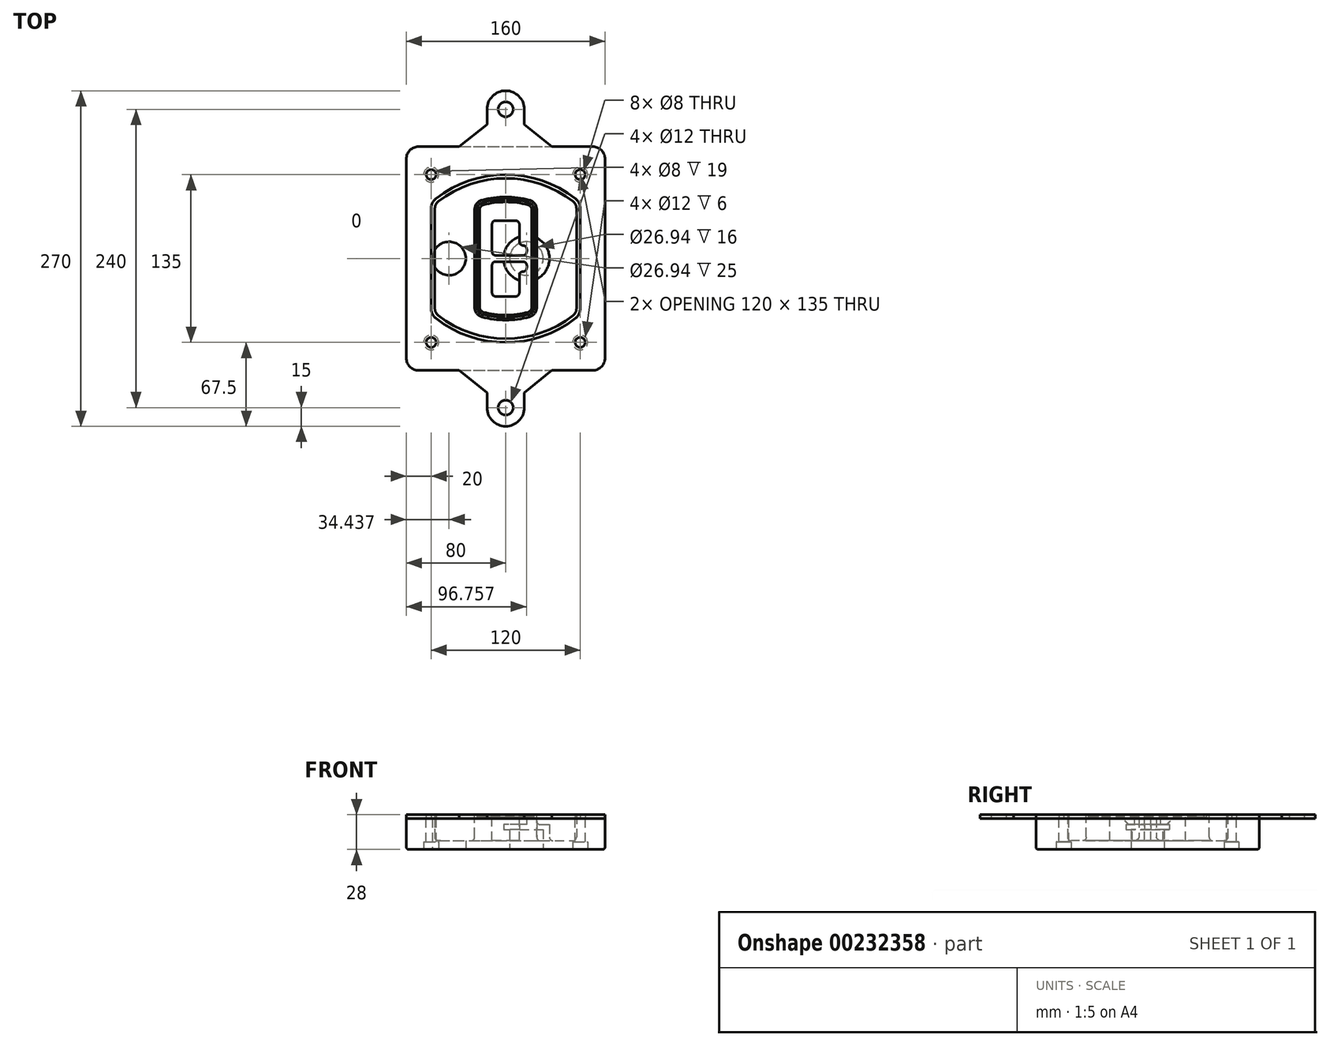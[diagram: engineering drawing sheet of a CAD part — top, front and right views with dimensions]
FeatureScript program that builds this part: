
annotation { "Feature Type Name" : "Feature", "Feature Type Description" : "" }
export const myFeature = defineFeature(function(context is Context, id is Id, definition is map)
    precondition{}
    {
        {
            var Q0;
            Q0=qCreatedBy(makeId("Top.planeOp"),FACE);
            var sketch = newSketch(context, id + "F0", { "sketchPlane" : qUnion([Q0])});
            skPoint(sketch, "E0.rect.middle", {"position": v(0, 0) * mm});
            skLineSegment(sketch, "E1.bottom", {"start": v(-70, -90) * mm, "end": v(70, -90) * mm});
            skLineSegment(sketch, "E1.top", {"start": v(-70, 90) * mm, "end": v(70, 90) * mm});
            skLineSegment(sketch, "E1.left", {"start": v(-80, -80) * mm, "end": v(-80, 80) * mm});
            skLineSegment(sketch, "E1.right", {"start": v(80, -80) * mm, "end": v(80, 80) * mm});
            skLineSegment(sketch, "E2", {"start": v(-80, 90) * mm, "end": v(80, -90) * mm, "construction": true});
            skLineSegment(sketch, "E3", {"start": v(80, 90) * mm, "end": v(-80, -90) * mm, "construction": true});
            skCircle(sketch, "E4", {"center": v(-60, 67.5) * mm, "radius": 4 * mm});
            skCircle(sketch, "E5", {"center": v(60, 67.5) * mm, "radius": 4 * mm});
            skCircle(sketch, "E6", {"center": v(60, -67.5) * mm, "radius": 4 * mm});
            skCircle(sketch, "E7", {"center": v(-60, -67.5) * mm, "radius": 4 * mm});
            skLineSegment(sketch, "E8", {"start": v(-60, 67.5) * mm, "end": v(60, 67.5) * mm, "construction": true});
            skLineSegment(sketch, "E9", {"start": v(60, 67.5) * mm, "end": v(60, -67.5) * mm, "construction": true});
            skLineSegment(sketch, "E10", {"start": v(60, -67.5) * mm, "end": v(-60, -67.5) * mm, "construction": true});
            skLineSegment(sketch, "E11", {"start": v(-60, -67.5) * mm, "end": v(-60, 67.5) * mm, "construction": true});
            skLineSegment(sketch, "E12", {"start": v(-60, 40.3) * mm, "end": v(-60, -40.3) * mm});
            skLineSegment(sketch, "E13", {"start": v(60, 40.3) * mm, "end": v(60, -40.3) * mm});
            skArc(sketch, "E14", {"start": v(56.15, 48.18) * mm, "mid": v(0, 67.5) * mm, "end": v(-56.15, 48.18) * mm});
            skArc(sketch, "E15", {"start": v(-56.15, -48.18) * mm, "mid": v(0, -67.5) * mm, "end": v(56.15, -48.18) * mm});
            skLineSegment(sketch, "E16", {"start": v(-60, 0) * mm, "end": v(60, 0) * mm, "construction": true});
            skPoint(sketch, "E17.visualSharp", {"position": v(-60, -45) * mm});
            skArc(sketch, "E17.filletArc", {"start": v(-60, -40.3) * mm, "mid": v(-58.99, -44.68) * mm, "end": v(-56.15, -48.18) * mm});
            skPoint(sketch, "E18.visualSharp", {"position": v(-60, 45) * mm});
            skArc(sketch, "E18.filletArc", {"start": v(-56.15, 48.18) * mm, "mid": v(-58.99, 44.68) * mm, "end": v(-60, 40.3) * mm});
            skPoint(sketch, "E19.visualSharp", {"position": v(60, 45) * mm});
            skArc(sketch, "E19.filletArc", {"start": v(60, 40.3) * mm, "mid": v(58.99, 44.68) * mm, "end": v(56.15, 48.18) * mm});
            skPoint(sketch, "E20.visualSharp", {"position": v(60, -45) * mm});
            skArc(sketch, "E20.filletArc", {"start": v(56.15, -48.18) * mm, "mid": v(58.99, -44.68) * mm, "end": v(60, -40.3) * mm});
            skPoint(sketch, "E21.visualSharp", {"position": v(-80, 90) * mm});
            skArc(sketch, "E21.filletArc", {"start": v(-70, 90) * mm, "mid": v(-77.07, 87.07) * mm, "end": v(-80, 80) * mm});
            skPoint(sketch, "E22.visualSharp", {"position": v(80, 90) * mm});
            skArc(sketch, "E22.filletArc", {"start": v(80, 80) * mm, "mid": v(77.07, 87.07) * mm, "end": v(70, 90) * mm});
            skPoint(sketch, "E23.visualSharp", {"position": v(80, -90) * mm});
            skArc(sketch, "E23.filletArc", {"start": v(70, -90) * mm, "mid": v(77.07, -87.07) * mm, "end": v(80, -80) * mm});
            skPoint(sketch, "E24.visualSharp", {"position": v(-80, -90) * mm});
            skArc(sketch, "E24.filletArc", {"start": v(-80, -80) * mm, "mid": v(-77.07, -87.07) * mm, "end": v(-70, -90) * mm});
            skArc(sketch, "E25.0", {"start": v(57, 40.3) * mm, "mid": v(56.3, 43.36) * mm, "end": v(54.3, 45.81) * mm});
            skLineSegment(sketch, "E25.1", {"start": v(57, 40.3) * mm, "end": v(57, -40.3) * mm});
            skArc(sketch, "E25.2", {"start": v(54.3, -45.81) * mm, "mid": v(56.3, -43.36) * mm, "end": v(57, -40.3) * mm});
            skArc(sketch, "E25.3", {"start": v(-54.3, -45.81) * mm, "mid": v(0, -64.5) * mm, "end": v(54.3, -45.81) * mm});
            skArc(sketch, "E25.4", {"start": v(-57, -40.3) * mm, "mid": v(-56.3, -43.36) * mm, "end": v(-54.3, -45.81) * mm});
            skArc(sketch, "E25.5", {"start": v(54.3, 45.81) * mm, "mid": v(0, 64.5) * mm, "end": v(-54.3, 45.81) * mm});
            skLineSegment(sketch, "E25.6", {"start": v(-57, 40.3) * mm, "end": v(-57, -40.3) * mm});
            skArc(sketch, "E25.7", {"start": v(-54.3, 45.81) * mm, "mid": v(-56.3, 43.36) * mm, "end": v(-57, 40.3) * mm});
            skArc(sketch, "E26.0", {"start": v(-58.62, 51.33) * mm, "mid": v(-62.58, 46.43) * mm, "end": v(-64, 40.3) * mm});
            skArc(sketch, "E26.1", {"start": v(58.62, 51.33) * mm, "mid": v(0, 71.5) * mm, "end": v(-58.62, 51.33) * mm});
            skArc(sketch, "E26.2", {"start": v(64, 40.3) * mm, "mid": v(62.58, 46.43) * mm, "end": v(58.62, 51.33) * mm});
            skLineSegment(sketch, "E26.3", {"start": v(64, 40.3) * mm, "end": v(64, -40.3) * mm});
            skArc(sketch, "E26.4", {"start": v(58.62, -51.33) * mm, "mid": v(62.58, -46.43) * mm, "end": v(64, -40.3) * mm});
            skLineSegment(sketch, "E26.5", {"start": v(-64, 40.3) * mm, "end": v(-64, -40.3) * mm});
            skArc(sketch, "E26.6", {"start": v(-58.62, -51.33) * mm, "mid": v(0, -71.5) * mm, "end": v(58.62, -51.33) * mm});
            skArc(sketch, "E26.7", {"start": v(-64, -40.3) * mm, "mid": v(-62.58, -46.43) * mm, "end": v(-58.62, -51.33) * mm});
            skSolve(sketch);
        }
        {
            var Q0;
            Q0=makeQuery(id+"F0.imprint","IMPRINT",FACE,{"disambiguationData":[TD([[makeQuery(id+"F0.imprint","IMPRINT",EDGE,{"derivedFrom":sQuery(id+"F0.wireOp",EDGE,"E1.bottom")}),1.0]])]});
            var Q1;
            Q1=makeQuery(id+"F0.imprint","IMPRINT",FACE,{"disambiguationData":[TD([[makeQuery(id+"F0.imprint","IMPRINT",EDGE,{"derivedFrom":sQuery(id+"F0.wireOp",EDGE,"E12")}),1.0]])]});
            var Q2;
            Q2=makeQuery(id+"F0.imprint","IMPRINT",FACE,{"disambiguationData":[TD([[makeQuery(id+"F0.imprint","IMPRINT",EDGE,{"derivedFrom":sQuery(id+"F0.wireOp",EDGE,"E25.0")}),1.0]])]});
            var Q3;
            Q3=makeQuery(id+"F0.imprint","IMPRINT",FACE,{"disambiguationData":[TD([[makeQuery(id+"F0.imprint","IMPRINT",EDGE,{"derivedFrom":sQuery(id+"F0.wireOp",EDGE,"E12")}),-1.0]])]});
            extrude(context, id + "F1", {"entities" : qUnion([Q0, Q1, Q2, Q3]), "oppositeDirection" : true, "depth" : 25 * mm});
        }
        {
            var Q0;
            Q0=makeQuery(id+"F0.imprint","IMPRINT",FACE,{"disambiguationData":[TD([[makeQuery(id+"F0.imprint","IMPRINT",EDGE,{"derivedFrom":sQuery(id+"F0.wireOp",EDGE,"E12")}),1.0]])]});
            extrude(context, id + "F2", {"entities" : qUnion([Q0]), "operationType" : NewBodyOperationType.ADD, "depth" : 3 * mm});
        }
        {
            var Q0;
            Q0=makeQuery(id+"F0.imprint","IMPRINT",FACE,{"disambiguationData":[TD([[makeQuery(id+"F0.imprint","IMPRINT",EDGE,{"derivedFrom":sQuery(id+"F0.wireOp",EDGE,"E25.0")}),1.0]])]});
            extrude(context, id + "F3", {"entities" : qUnion([Q0]), "operationType" : NewBodyOperationType.REMOVE, "oppositeDirection" : true, "depth" : 18 * mm});
        }
        {
            var Q0;
            Q0=makeQuery(id+"F2.opExtrude","CAP_FACE",FACE,{"disambiguationData":[OSD([sQuery(id+"F0.wireOp",EDGE,"E12"),sQuery(id+"F0.wireOp",EDGE,"E13"),sQuery(id+"F0.wireOp",EDGE,"E14"),sQuery(id+"F0.wireOp",EDGE,"E15"),sQuery(id+"F0.wireOp",EDGE,"E17.filletArc"),sQuery(id+"F0.wireOp",EDGE,"E18.filletArc"),sQuery(id+"F0.wireOp",EDGE,"E19.filletArc"),sQuery(id+"F0.wireOp",EDGE,"E20.filletArc"),sQuery(id+"F0.wireOp",EDGE,"E25.0"),sQuery(id+"F0.wireOp",EDGE,"E25.1"),sQuery(id+"F0.wireOp",EDGE,"E25.2"),sQuery(id+"F0.wireOp",EDGE,"E25.3"),sQuery(id+"F0.wireOp",EDGE,"E25.4"),sQuery(id+"F0.wireOp",EDGE,"E25.5"),sQuery(id+"F0.wireOp",EDGE,"E25.6"),sQuery(id+"F0.wireOp",EDGE,"E25.7")])],"isStart":false});
            var sketch = newSketch(context, id + "F4", { "sketchPlane" : qUnion([Q0])});
            skArc(sketch, "E27.0", {"start": v(-19.08, -46.97) * mm, "mid": v(0, -49.5) * mm, "end": v(19.08, -46.97) * mm});
            skArc(sketch, "E28.0", {"start": v(19.08, 46.97) * mm, "mid": v(0, 49.5) * mm, "end": v(-19.08, 46.97) * mm});
            skLineSegment(sketch, "E29", {"start": v(-25, 39.25) * mm, "end": v(-25, -39.25) * mm});
            skLineSegment(sketch, "E30", {"start": v(25, 39.25) * mm, "end": v(25, -39.25) * mm});
            skLineSegment(sketch, "E31", {"start": v(-25, 45.1) * mm, "end": v(25, 45.1) * mm, "construction": true});
            skLineSegment(sketch, "E32", {"start": v(-25, -45.1) * mm, "end": v(25, -45.1) * mm, "construction": true});
            skPoint(sketch, "E33.visualSharp", {"position": v(-25, 45.1) * mm});
            skArc(sketch, "E33.filletArc", {"start": v(-19.08, 46.97) * mm, "mid": v(-23.35, 44.11) * mm, "end": v(-25, 39.25) * mm});
            skPoint(sketch, "E34.visualSharp", {"position": v(25, 45.1) * mm});
            skArc(sketch, "E34.filletArc", {"start": v(25, 39.25) * mm, "mid": v(23.35, 44.11) * mm, "end": v(19.08, 46.97) * mm});
            skPoint(sketch, "E35.visualSharp", {"position": v(25, -45.1) * mm});
            skArc(sketch, "E35.filletArc", {"start": v(19.08, -46.97) * mm, "mid": v(23.35, -44.11) * mm, "end": v(25, -39.25) * mm});
            skPoint(sketch, "E36.visualSharp", {"position": v(-25, -45.1) * mm});
            skArc(sketch, "E36.filletArc", {"start": v(-25, -39.25) * mm, "mid": v(-23.35, -44.11) * mm, "end": v(-19.08, -46.97) * mm});
            skArc(sketch, "E37.0", {"start": v(54.3, 45.81) * mm, "mid": v(0, 64.5) * mm, "end": v(-54.3, 45.81) * mm});
            skArc(sketch, "E37.1", {"start": v(-54.3, 45.81) * mm, "mid": v(-56.3, 43.36) * mm, "end": v(-57, 40.3) * mm});
            skLineSegment(sketch, "E37.2", {"start": v(-57, 40.3) * mm, "end": v(-57, -40.3) * mm});
            skArc(sketch, "E37.3", {"start": v(-57, -40.3) * mm, "mid": v(-56.3, -43.36) * mm, "end": v(-54.3, -45.81) * mm});
            skArc(sketch, "E37.4", {"start": v(-54.3, -45.81) * mm, "mid": v(0, -64.5) * mm, "end": v(54.3, -45.81) * mm});
            skArc(sketch, "E37.5", {"start": v(54.3, -45.81) * mm, "mid": v(56.3, -43.36) * mm, "end": v(57, -40.3) * mm});
            skLineSegment(sketch, "E37.6", {"start": v(57, 40.3) * mm, "end": v(57, -40.3) * mm});
            skArc(sketch, "E37.7", {"start": v(57, 40.3) * mm, "mid": v(56.3, 43.36) * mm, "end": v(54.3, 45.81) * mm});
            skLineSegment(sketch, "E38.0", {"start": v(23, 39.25) * mm, "end": v(23, -39.25) * mm});
            skArc(sketch, "E38.1", {"start": v(18.56, -45.04) * mm, "mid": v(21.76, -42.9) * mm, "end": v(23, -39.25) * mm});
            skArc(sketch, "E38.2", {"start": v(-18.56, -45.04) * mm, "mid": v(0, -47.5) * mm, "end": v(18.56, -45.04) * mm});
            skArc(sketch, "E38.3", {"start": v(-23, -39.25) * mm, "mid": v(-21.76, -42.9) * mm, "end": v(-18.56, -45.04) * mm});
            skLineSegment(sketch, "E38.4", {"start": v(-23, 39.25) * mm, "end": v(-23, -39.25) * mm});
            skArc(sketch, "E38.5", {"start": v(23, 39.25) * mm, "mid": v(21.76, 42.9) * mm, "end": v(18.56, 45.04) * mm});
            skArc(sketch, "E38.6", {"start": v(-18.56, 45.04) * mm, "mid": v(-21.76, 42.9) * mm, "end": v(-23, 39.25) * mm});
            skArc(sketch, "E38.7", {"start": v(18.56, 45.04) * mm, "mid": v(0, 47.5) * mm, "end": v(-18.56, 45.04) * mm});
            skArc(sketch, "E39.0", {"start": v(21, 39.25) * mm, "mid": v(20.18, 41.68) * mm, "end": v(18.04, 43.1) * mm});
            skLineSegment(sketch, "E39.1", {"start": v(21, 39.25) * mm, "end": v(21, -39.25) * mm});
            skArc(sketch, "E39.2", {"start": v(18.04, -43.1) * mm, "mid": v(20.18, -41.68) * mm, "end": v(21, -39.25) * mm});
            skArc(sketch, "E39.3", {"start": v(-18.04, -43.1) * mm, "mid": v(0, -45.5) * mm, "end": v(18.04, -43.1) * mm});
            skArc(sketch, "E39.4", {"start": v(-21, -39.25) * mm, "mid": v(-20.18, -41.68) * mm, "end": v(-18.04, -43.1) * mm});
            skArc(sketch, "E39.5", {"start": v(18.04, 43.1) * mm, "mid": v(0, 45.5) * mm, "end": v(-18.04, 43.1) * mm});
            skLineSegment(sketch, "E39.6", {"start": v(-21, 39.25) * mm, "end": v(-21, -39.25) * mm});
            skArc(sketch, "E39.7", {"start": v(-18.04, 43.1) * mm, "mid": v(-20.18, 41.68) * mm, "end": v(-21, 39.25) * mm});
            skLineSegment(sketch, "E40", {"start": v(-25, 0) * mm, "end": v(25, 0) * mm, "construction": true});
            skLineSegment(sketch, "E41", {"start": v(-11, 5.5) * mm, "end": v(-11, 27.5) * mm});
            skLineSegment(sketch, "E42", {"start": v(-8, 30.5) * mm, "end": v(8, 30.5) * mm});
            skLineSegment(sketch, "E43", {"start": v(11, 27.5) * mm, "end": v(11, 13.5) * mm});
            skLineSegment(sketch, "E44", {"start": v(14, 10.5) * mm, "end": v(14, 10.5) * mm});
            skLineSegment(sketch, "E45", {"start": v(17, 7.5) * mm, "end": v(17, 5.5) * mm});
            skLineSegment(sketch, "E46", {"start": v(14, 2.5) * mm, "end": v(-8, 2.5) * mm});
            skPoint(sketch, "E47.visualSharp", {"position": v(-11, 30.5) * mm});
            skArc(sketch, "E47.filletArc", {"start": v(-8, 30.5) * mm, "mid": v(-10.12, 29.62) * mm, "end": v(-11, 27.5) * mm});
            skPoint(sketch, "E48.visualSharp", {"position": v(11, 30.5) * mm});
            skArc(sketch, "E48.filletArc", {"start": v(11, 27.5) * mm, "mid": v(10.12, 29.62) * mm, "end": v(8, 30.5) * mm});
            skPoint(sketch, "E49.visualSharp", {"position": v(11, 10.5) * mm});
            skArc(sketch, "E49.filletArc", {"start": v(11, 13.5) * mm, "mid": v(11.88, 11.38) * mm, "end": v(14, 10.5) * mm});
            skPoint(sketch, "E50.visualSharp", {"position": v(17, 10.5) * mm});
            skArc(sketch, "E50.filletArc", {"start": v(17, 7.5) * mm, "mid": v(16.12, 9.62) * mm, "end": v(14, 10.5) * mm});
            skPoint(sketch, "E51.visualSharp", {"position": v(17, 2.5) * mm});
            skArc(sketch, "E51.filletArc", {"start": v(14, 2.5) * mm, "mid": v(16.12, 3.38) * mm, "end": v(17, 5.5) * mm});
            skPoint(sketch, "E52.visualSharp", {"position": v(-11, 2.5) * mm});
            skArc(sketch, "E52.filletArc", {"start": v(-11, 5.5) * mm, "mid": v(-10.12, 3.38) * mm, "end": v(-8, 2.5) * mm});
            skLineSegment(sketch, "E53.0.MirrorCS", {"start": v(14, -2.5) * mm, "end": v(-8, -2.5) * mm});
            skArc(sketch, "E54.0.MirrorCS", {"start": v(-11, -5.5) * mm, "mid": v(-10.12, -3.38) * mm, "end": v(-8, -2.5) * mm});
            skLineSegment(sketch, "E55.0.MirrorCS", {"start": v(-11, -5.5) * mm, "end": v(-11, -27.5) * mm});
            skArc(sketch, "E56.0.MirrorCS", {"start": v(-8, -30.5) * mm, "mid": v(-10.12, -29.62) * mm, "end": v(-11, -27.5) * mm});
            skLineSegment(sketch, "E57.0.MirrorCS", {"start": v(-8, -30.5) * mm, "end": v(8, -30.5) * mm});
            skArc(sketch, "E58.0.MirrorCS", {"start": v(11, -27.5) * mm, "mid": v(10.12, -29.62) * mm, "end": v(8, -30.5) * mm});
            skLineSegment(sketch, "E59.0.MirrorCS", {"start": v(11, -27.5) * mm, "end": v(11, -13.5) * mm});
            skArc(sketch, "E60.0.MirrorCS", {"start": v(11, -13.5) * mm, "mid": v(11.88, -11.38) * mm, "end": v(14, -10.5) * mm});
            skArc(sketch, "E61.0.MirrorCS", {"start": v(17, -7.5) * mm, "mid": v(16.12, -9.62) * mm, "end": v(14, -10.5) * mm});
            skLineSegment(sketch, "E62.0.MirrorCS", {"start": v(17, -7.5) * mm, "end": v(17, -5.5) * mm});
            skArc(sketch, "E63.0.MirrorCS", {"start": v(14, -2.5) * mm, "mid": v(16.12, -3.38) * mm, "end": v(17, -5.5) * mm});
            skSolve(sketch);
        }
        {
            var Q0;
            Q0=makeQuery(id+"F4.imprint","IMPRINT",FACE,{"disambiguationData":[TD([[makeQuery(id+"F4.imprint","IMPRINT",EDGE,{"derivedFrom":sQuery(id+"F4.wireOp",EDGE,"E27.0")}),1.0]])]});
            var Q1;
            Q1=makeQuery(id+"F4.imprint","IMPRINT",FACE,{"disambiguationData":[TD([[makeQuery(id+"F4.imprint","IMPRINT",EDGE,{"derivedFrom":sQuery(id+"F4.wireOp",EDGE,"E38.0")}),-1.0]])]});
            var Q2;
            Q2=makeQuery(id+"F4.imprint","IMPRINT",FACE,{"disambiguationData":[TD([[makeQuery(id+"F4.imprint","IMPRINT",EDGE,{"derivedFrom":sQuery(id+"F4.wireOp",EDGE,"E39.0")}),1.0]])]});
            extrude(context, id + "F5", {"entities" : qUnion([Q0, Q1, Q2]), "operationType" : NewBodyOperationType.ADD, "endBound" : BoundingType.UP_TO_NEXT, "oppositeDirection" : true, "depth" : 25 * mm});
        }
        {
            var Q0;
            Q0=makeQuery(id+"F4.imprint","IMPRINT",FACE,{"disambiguationData":[TD([[makeQuery(id+"F4.imprint","IMPRINT",EDGE,{"derivedFrom":sQuery(id+"F4.wireOp",EDGE,"E38.0")}),-1.0]])]});
            extrude(context, id + "F6", {"entities" : qUnion([Q0]), "operationType" : NewBodyOperationType.REMOVE, "oppositeDirection" : true, "depth" : 2 * mm});
        }
        {
            var Q0;
            Q0=makeQuery(id+"F1.opExtrude","CAP_FACE",FACE,{"disambiguationData":[OSD([sQuery(id+"F0.wireOp",EDGE,"E1.bottom"),sQuery(id+"F0.wireOp",EDGE,"E1.top"),sQuery(id+"F0.wireOp",EDGE,"E1.left"),sQuery(id+"F0.wireOp",EDGE,"E1.right"),sQuery(id+"F0.wireOp",EDGE,"E4"),sQuery(id+"F0.wireOp",EDGE,"E5"),sQuery(id+"F0.wireOp",EDGE,"E6"),sQuery(id+"F0.wireOp",EDGE,"E7"),sQuery(id+"F0.wireOp",EDGE,"E21.filletArc"),sQuery(id+"F0.wireOp",EDGE,"E22.filletArc"),sQuery(id+"F0.wireOp",EDGE,"E23.filletArc"),sQuery(id+"F0.wireOp",EDGE,"E24.filletArc")])],"isStart":false});
            var sketch = newSketch(context, id + "F7", { "sketchPlane" : qUnion([Q0])});
            skCircle(sketch, "E64", {"center": v(16.76, 0) * mm, "radius": 13.47 * mm});
            skCircle(sketch, "E65", {"center": v(-45.56, 0) * mm, "radius": 13.47 * mm});
            skLineSegment(sketch, "E66", {"start": v(80, 0) * mm, "end": v(-80, 0) * mm});
            skCircle(sketch, "E67", {"center": v(16.76, 0) * mm, "radius": 18.47 * mm});
            skCircle(sketch, "E68", {"center": v(60, -67.5) * mm, "radius": 6 * mm});
            skCircle(sketch, "E69", {"center": v(-60, -67.5) * mm, "radius": 6 * mm});
            skCircle(sketch, "E70", {"center": v(-60, 67.5) * mm, "radius": 6 * mm});
            skCircle(sketch, "E71", {"center": v(60, 67.5) * mm, "radius": 6 * mm});
            skSolve(sketch);
        }
        {
            var Q0;
            {var subQ1=sQuery(id+"F7.wireOp",EDGE,"E66");var subQ4=sQuery(id+"F7.wireOp",EDGE,"E64");var subQ6=makeQuery(id+"F7.imprint","INTERSECT",VERTEX,{"disambiguationData":[OD(0.0)],"derivedFrom":[subQ4,subQ1]});Q0=makeQuery(id+"F7.imprint","IMPRINT",FACE,{"disambiguationData":[TD([[makeQuery(id+"F7.imprint","IMPRINT",EDGE,{"disambiguationData":[TD([[subQ6,-1.0]])],"derivedFrom":subQ4}),-1.0]])]});}
            var Q1;
            {var subQ0=sQuery(id+"F7.wireOp",EDGE,"E66");var subQ1=sQuery(id+"F7.wireOp",EDGE,"E64");var subQ3=makeQuery(id+"F7.imprint","INTERSECT",VERTEX,{"disambiguationData":[OD(0.0)],"derivedFrom":[subQ1,subQ0]});Q1=makeQuery(id+"F7.imprint","IMPRINT",FACE,{"disambiguationData":[TD([[makeQuery(id+"F7.imprint","IMPRINT",EDGE,{"disambiguationData":[TD([[subQ3,-1.0]])],"derivedFrom":subQ1}),1.0]])]});}
            var Q2;
            {var subQ0=sQuery(id+"F7.wireOp",EDGE,"E66");var subQ1=sQuery(id+"F7.wireOp",EDGE,"E64");var subQ3=makeQuery(id+"F7.imprint","INTERSECT",VERTEX,{"disambiguationData":[OD(0.0)],"derivedFrom":[subQ1,subQ0]});Q2=makeQuery(id+"F7.imprint","IMPRINT",FACE,{"disambiguationData":[TD([[makeQuery(id+"F7.imprint","IMPRINT",EDGE,{"disambiguationData":[TD([[subQ3,1.0]])],"derivedFrom":subQ1}),1.0]])]});}
            var Q3;
            {var subQ1=sQuery(id+"F7.wireOp",EDGE,"E66");var subQ4=sQuery(id+"F7.wireOp",EDGE,"E64");var subQ6=makeQuery(id+"F7.imprint","INTERSECT",VERTEX,{"disambiguationData":[OD(0.0)],"derivedFrom":[subQ4,subQ1]});Q3=makeQuery(id+"F7.imprint","IMPRINT",FACE,{"disambiguationData":[TD([[makeQuery(id+"F7.imprint","IMPRINT",EDGE,{"disambiguationData":[TD([[subQ6,1.0]])],"derivedFrom":subQ4}),-1.0]])]});}
            extrude(context, id + "F8", {"entities" : qUnion([Q0, Q1, Q2, Q3]), "operationType" : NewBodyOperationType.ADD, "oppositeDirection" : true, "depth" : 20 * mm});
        }
        {
            var Q0;
            {var subQ0=sQuery(id+"F7.wireOp",EDGE,"E66");var subQ1=sQuery(id+"F7.wireOp",EDGE,"E64");var subQ3=makeQuery(id+"F7.imprint","INTERSECT",VERTEX,{"disambiguationData":[OD(0.0)],"derivedFrom":[subQ1,subQ0]});Q0=makeQuery(id+"F7.imprint","IMPRINT",FACE,{"disambiguationData":[TD([[makeQuery(id+"F7.imprint","IMPRINT",EDGE,{"disambiguationData":[TD([[subQ3,-1.0]])],"derivedFrom":subQ1}),1.0]])]});}
            var Q1;
            {var subQ0=sQuery(id+"F7.wireOp",EDGE,"E66");var subQ1=sQuery(id+"F7.wireOp",EDGE,"E64");var subQ3=makeQuery(id+"F7.imprint","INTERSECT",VERTEX,{"disambiguationData":[OD(0.0)],"derivedFrom":[subQ1,subQ0]});Q1=makeQuery(id+"F7.imprint","IMPRINT",FACE,{"disambiguationData":[TD([[makeQuery(id+"F7.imprint","IMPRINT",EDGE,{"disambiguationData":[TD([[subQ3,1.0]])],"derivedFrom":subQ1}),1.0]])]});}
            extrude(context, id + "F9", {"entities" : qUnion([Q0, Q1]), "operationType" : NewBodyOperationType.REMOVE, "oppositeDirection" : true, "depth" : 16 * mm});
        }
        {
            var Q0;
            {var subQ0=sQuery(id+"F7.wireOp",EDGE,"E66");var subQ1=sQuery(id+"F7.wireOp",EDGE,"E65");var subQ3=makeQuery(id+"F7.imprint","INTERSECT",VERTEX,{"disambiguationData":[OD(0.0)],"derivedFrom":[subQ1,subQ0]});Q0=makeQuery(id+"F7.imprint","IMPRINT",FACE,{"disambiguationData":[TD([[makeQuery(id+"F7.imprint","IMPRINT",EDGE,{"disambiguationData":[TD([[subQ3,-1.0]])],"derivedFrom":subQ1}),1.0]])]});}
            var Q1;
            {var subQ0=sQuery(id+"F7.wireOp",EDGE,"E66");var subQ1=sQuery(id+"F7.wireOp",EDGE,"E65");var subQ3=makeQuery(id+"F7.imprint","INTERSECT",VERTEX,{"disambiguationData":[OD(0.0)],"derivedFrom":[subQ1,subQ0]});Q1=makeQuery(id+"F7.imprint","IMPRINT",FACE,{"disambiguationData":[TD([[makeQuery(id+"F7.imprint","IMPRINT",EDGE,{"disambiguationData":[TD([[subQ3,1.0]])],"derivedFrom":subQ1}),1.0]])]});}
            extrude(context, id + "F10", {"entities" : qUnion([Q0, Q1]), "operationType" : NewBodyOperationType.REMOVE, "oppositeDirection" : true, "depth" : 25 * mm});
        }
        {
            var Q0;
            Q0=makeQuery(id+"F7.imprint","IMPRINT",FACE,{"disambiguationData":[TD([[makeQuery(id+"F7.imprint","IMPRINT",EDGE,{"derivedFrom":sQuery(id+"F7.wireOp",EDGE,"E68")}),1.0]])]});
            var Q1;
            Q1=makeQuery(id+"F7.imprint","IMPRINT",FACE,{"disambiguationData":[TD([[makeQuery(id+"F7.imprint","IMPRINT",EDGE,{"derivedFrom":makeQuery(id+"F1.opExtrude","CAP_EDGE",EDGE,{"disambiguationData":[OSD([sQuery(id+"F0.wireOp",EDGE,"E5")])],"isStart":false})}),-1.0]])]});
            var Q2;
            Q2=makeQuery(id+"F7.imprint","IMPRINT",FACE,{"disambiguationData":[TD([[makeQuery(id+"F7.imprint","IMPRINT",EDGE,{"derivedFrom":sQuery(id+"F7.wireOp",EDGE,"E69")}),1.0]])]});
            var Q3;
            Q3=makeQuery(id+"F7.imprint","IMPRINT",FACE,{"disambiguationData":[TD([[makeQuery(id+"F7.imprint","IMPRINT",EDGE,{"derivedFrom":makeQuery(id+"F1.opExtrude","CAP_EDGE",EDGE,{"disambiguationData":[OSD([sQuery(id+"F0.wireOp",EDGE,"E4")])],"isStart":false})}),-1.0]])]});
            var Q4;
            Q4=makeQuery(id+"F7.imprint","IMPRINT",FACE,{"disambiguationData":[TD([[makeQuery(id+"F7.imprint","IMPRINT",EDGE,{"derivedFrom":sQuery(id+"F7.wireOp",EDGE,"E70")}),1.0]])]});
            var Q5;
            Q5=makeQuery(id+"F7.imprint","IMPRINT",FACE,{"disambiguationData":[TD([[makeQuery(id+"F7.imprint","IMPRINT",EDGE,{"derivedFrom":makeQuery(id+"F1.opExtrude","CAP_EDGE",EDGE,{"disambiguationData":[OSD([sQuery(id+"F0.wireOp",EDGE,"E7")])],"isStart":false})}),-1.0]])]});
            var Q6;
            Q6=makeQuery(id+"F7.imprint","IMPRINT",FACE,{"disambiguationData":[TD([[makeQuery(id+"F7.imprint","IMPRINT",EDGE,{"derivedFrom":sQuery(id+"F7.wireOp",EDGE,"E71")}),1.0]])]});
            var Q7;
            Q7=makeQuery(id+"F7.imprint","IMPRINT",FACE,{"disambiguationData":[TD([[makeQuery(id+"F7.imprint","IMPRINT",EDGE,{"derivedFrom":makeQuery(id+"F1.opExtrude","CAP_EDGE",EDGE,{"disambiguationData":[OSD([sQuery(id+"F0.wireOp",EDGE,"E6")])],"isStart":false})}),-1.0]])]});
            extrude(context, id + "F11", {"entities" : qUnion([Q0, Q1, Q2, Q3, Q4, Q5, Q6, Q7]), "operationType" : NewBodyOperationType.REMOVE, "oppositeDirection" : true, "depth" : 6 * mm});
        }
        {
            var Q0;
            Q0=makeQuery(id+"F9.boolean.opBoolean","COPY",FACE,{"derivedFrom":makeQuery(id+"F9.opExtrude","CAP_FACE",FACE,{"disambiguationData":[OSD([sQuery(id+"F7.wireOp",EDGE,"E64")])],"isStart":false})});
            var sketch = newSketch(context, id + "F12", { "sketchPlane" : qUnion([Q0])});
            skArc(sketch, "E72.0", {"start": v(11, 17.55) * mm, "mid": v(2.57, 11.82) * mm, "end": v(-1.54, 2.5) * mm});
            skArc(sketch, "E72.1", {"start": v(-1.54, -2.5) * mm, "mid": v(2.57, -11.82) * mm, "end": v(11, -17.55) * mm});
            skLineSegment(sketch, "E73", {"start": v(-1.54, -2.5) * mm, "end": v(14, -2.5) * mm});
            skLineSegment(sketch, "E74.0", {"start": v(14, 2.5) * mm, "end": v(-1.54, 2.5) * mm});
            skArc(sketch, "E74.1", {"start": v(14, 2.5) * mm, "mid": v(16.12, 3.38) * mm, "end": v(17, 5.5) * mm});
            skLineSegment(sketch, "E74.2", {"start": v(17, 7.5) * mm, "end": v(17, 5.5) * mm});
            skArc(sketch, "E74.3", {"start": v(17, 7.5) * mm, "mid": v(16.12, 9.62) * mm, "end": v(14, 10.5) * mm});
            skArc(sketch, "E74.4", {"start": v(11, 13.5) * mm, "mid": v(11.88, 11.38) * mm, "end": v(14, 10.5) * mm});
            skLineSegment(sketch, "E74.5", {"start": v(11, 17.55) * mm, "end": v(11, 13.5) * mm});
            skLineSegment(sketch, "E74.7", {"start": v(14, -2.5) * mm, "end": v(-1.54, -2.5) * mm});
            skArc(sketch, "E74.8", {"start": v(14, -2.5) * mm, "mid": v(16.12, -3.38) * mm, "end": v(17, -5.5) * mm});
            skLineSegment(sketch, "E74.9", {"start": v(17, -7.5) * mm, "end": v(17, -5.5) * mm});
            skArc(sketch, "E74.10", {"start": v(17, -7.5) * mm, "mid": v(16.12, -9.62) * mm, "end": v(14, -10.5) * mm});
            skArc(sketch, "E74.11", {"start": v(11, -13.5) * mm, "mid": v(11.88, -11.38) * mm, "end": v(14, -10.5) * mm});
            skLineSegment(sketch, "E74.12", {"start": v(11, -17.55) * mm, "end": v(11, -13.5) * mm});
            skPoint(sketch, "E75.orphan", {"position": v(11, -27.5) * mm});
            skPoint(sketch, "E76.orphan", {"position": v(-8, -2.5) * mm});
            skPoint(sketch, "E77.orphan", {"position": v(-8, 2.5) * mm});
            skPoint(sketch, "E78.orphan", {"position": v(11, 27.5) * mm});
            skSolve(sketch);
        }
        {
            var Q0;
            {var subQ7=sQuery(id+"F12.wireOp",EDGE,"E72.0");var subQ14=sQuery(id+"F12.wireOp",EDGE,"E72.1");var subQ16=sQuery(id+"F12.wireOp",EDGE,"E74.1");var subQ18=sQuery(id+"F12.wireOp",EDGE,"E74.8");Q0=qUnion([makeQuery(id+"F12.imprint","IMPRINT",FACE,{"disambiguationData":[TD([[makeQuery(id+"F12.imprint","IMPRINT",EDGE,{"derivedFrom":subQ7}),1.0]])]}),makeQuery(id+"F12.imprint","IMPRINT",FACE,{"disambiguationData":[TD([[makeQuery(id+"F12.imprint","IMPRINT",EDGE,{"derivedFrom":subQ14}),1.0]])]}),makeQuery(id+"F12.imprint","IMPRINT",FACE,{"disambiguationData":[TD([[makeQuery(id+"F12.imprint","IMPRINT",EDGE,{"derivedFrom":subQ16}),1.0]])]}),makeQuery(id+"F12.imprint","IMPRINT",FACE,{"disambiguationData":[TD([[makeQuery(id+"F12.imprint","IMPRINT",EDGE,{"derivedFrom":subQ18}),-1.0]])]})]);}
            var Q1;
            Q1=makeQuery(id+"F5.boolean.opBoolean","SPLIT",FACE,{"disambiguationData":[TD([makeQuery(id+"F5.opExtrude","SWEPT_FACE",FACE,{"disambiguationData":[OSD([sQuery(id+"F4.wireOp",EDGE,"E41")])]})])],"derivedFrom":makeQuery(id+"F3.boolean.opBoolean","COPY",FACE,{"derivedFrom":makeQuery(id+"F3.opExtrude","CAP_FACE",FACE,{"disambiguationData":[OSD([sQuery(id+"F0.wireOp",EDGE,"E25.0"),sQuery(id+"F0.wireOp",EDGE,"E25.1"),sQuery(id+"F0.wireOp",EDGE,"E25.2"),sQuery(id+"F0.wireOp",EDGE,"E25.3"),sQuery(id+"F0.wireOp",EDGE,"E25.4"),sQuery(id+"F0.wireOp",EDGE,"E25.5"),sQuery(id+"F0.wireOp",EDGE,"E25.6"),sQuery(id+"F0.wireOp",EDGE,"E25.7")])],"isStart":false})})});
            extrude(context, id + "F13", {"entities" : qUnion([Q0]), "operationType" : NewBodyOperationType.REMOVE, "endBound" : BoundingType.UP_TO_SURFACE, "endBoundEntityFace" : qUnion([Q1]), "depth" : 25 * mm});
        }
        {
            var Q0;
            Q0=makeQuery(id+"F3.boolean.opBoolean","COPY",EDGE,{"derivedFrom":makeQuery(id+"F3.opExtrude","CAP_EDGE",EDGE,{"disambiguationData":[OSD([sQuery(id+"F0.wireOp",EDGE,"E25.6")])],"isStart":false})});
            var Q1;
            Q1=makeQuery(id+"F8.boolean.opBoolean","INTERSECT",EDGE,{"derivedFrom":[makeQuery(id+"F5.opExtrude","SWEPT_FACE",FACE,{"disambiguationData":[OSD([sQuery(id+"F4.wireOp",EDGE,"E30")])]}),makeQuery(id+"F8.opExtrude","CAP_FACE",FACE,{"disambiguationData":[OSD([sQuery(id+"F7.wireOp",EDGE,"E67")])],"isStart":false})]});
            var Q2;
            Q2=makeQuery(id+"F8.boolean.opBoolean","INTERSECT",EDGE,{"disambiguationData":[OD(1.0)],"derivedFrom":[makeQuery(id+"F5.opExtrude","SWEPT_FACE",FACE,{"disambiguationData":[OSD([sQuery(id+"F4.wireOp",EDGE,"E30")])]}),makeQuery(id+"F8.opExtrude","SWEPT_FACE",FACE,{"disambiguationData":[OSD([sQuery(id+"F7.wireOp",EDGE,"E67")])]})]});
            var Q3;
            {var subQ0=sQuery(id+"F4.wireOp",EDGE,"E30");Q3=makeQuery(id+"F8.boolean.opBoolean","SPLIT",EDGE,{"disambiguationData":[TD([makeQuery(id+"F5.opExtrude","SWEPT_FACE",FACE,{"disambiguationData":[OSD([sQuery(id+"F4.wireOp",EDGE,"E35.filletArc")])]})])],"derivedFrom":makeQuery(id+"F5.opExtrude","CAP_EDGE",EDGE,{"disambiguationData":[OSD([subQ0])],"isStart":false})});}
            var Q4;
            {var subQ0=sQuery(id+"F0.wireOp",EDGE,"E25.7");var subQ1=sQuery(id+"F0.wireOp",EDGE,"E25.1");var subQ2=sQuery(id+"F0.wireOp",EDGE,"E25.6");var subQ3=sQuery(id+"F0.wireOp",EDGE,"E25.5");var subQ4=sQuery(id+"F0.wireOp",EDGE,"E25.4");var subQ5=sQuery(id+"F0.wireOp",EDGE,"E25.0");var subQ6=sQuery(id+"F0.wireOp",EDGE,"E25.2");var subQ7=sQuery(id+"F0.wireOp",EDGE,"E25.3");Q4=makeQuery(id+"F8.boolean.opBoolean","INTERSECT",EDGE,{"derivedFrom":[makeQuery(id+"F5.boolean.opBoolean","SPLIT",FACE,{"disambiguationData":[TD([makeQuery(id+"F2.opExtrude","SWEPT_FACE",FACE,{"disambiguationData":[OSD([subQ5])]})])],"derivedFrom":makeQuery(id+"F3.boolean.opBoolean","COPY",FACE,{"derivedFrom":makeQuery(id+"F3.opExtrude","CAP_FACE",FACE,{"disambiguationData":[OSD([subQ5,subQ1,subQ6,subQ7,subQ4,subQ3,subQ2,subQ0])],"isStart":false})})}),makeQuery(id+"F8.opExtrude","SWEPT_FACE",FACE,{"disambiguationData":[OSD([sQuery(id+"F7.wireOp",EDGE,"E67")])]})]});}
            var Q5;
            Q5=makeQuery(id+"F8.boolean.opBoolean","INTERSECT",EDGE,{"disambiguationData":[OD(0.0)],"derivedFrom":[makeQuery(id+"F5.opExtrude","SWEPT_FACE",FACE,{"disambiguationData":[OSD([sQuery(id+"F4.wireOp",EDGE,"E30")])]}),makeQuery(id+"F8.opExtrude","SWEPT_FACE",FACE,{"disambiguationData":[OSD([sQuery(id+"F7.wireOp",EDGE,"E67")])]})]});
            fillet(context, id + "F14", {"entities" : qUnion([Q0, Q1, Q2, Q3, Q4, Q5]), "radius" : 3 * mm, "tangentPropagation" : true, "allowEdgeOverflow" : false});
        }
        {
            var Q0;
            Q0=makeQuery(id+"F1.opExtrude","CAP_EDGE",EDGE,{"disambiguationData":[OSD([sQuery(id+"F0.wireOp",EDGE,"E1.bottom")])],"isStart":false});
            fillet(context, id + "F15", {"entities" : qUnion([Q0]), "radius" : 2 * mm, "tangentPropagation" : true, "allowEdgeOverflow" : false});
        }
        {
            var Q0;
            {var subQ0=sQuery(id+"F0.wireOp",EDGE,"E22.filletArc");var subQ1=sQuery(id+"F0.wireOp",EDGE,"E7");var subQ2=sQuery(id+"F0.wireOp",EDGE,"E6");var subQ3=sQuery(id+"F0.wireOp",EDGE,"E5");var subQ4=sQuery(id+"F0.wireOp",EDGE,"E4");var subQ5=sQuery(id+"F0.wireOp",EDGE,"E1.bottom");var subQ6=sQuery(id+"F0.wireOp",EDGE,"E21.filletArc");var subQ7=sQuery(id+"F0.wireOp",EDGE,"E1.top");var subQ8=sQuery(id+"F0.wireOp",EDGE,"E1.left");var subQ9=sQuery(id+"F0.wireOp",EDGE,"E1.right");var subQ10=sQuery(id+"F0.wireOp",EDGE,"E23.filletArc");var subQ11=sQuery(id+"F0.wireOp",EDGE,"E24.filletArc");Q0=makeQuery(id+"F2.boolean.opBoolean","SPLIT",FACE,{"disambiguationData":[TD([makeQuery(id+"F1.opExtrude","SWEPT_FACE",FACE,{"disambiguationData":[OSD([subQ5])]})])],"derivedFrom":makeQuery(id+"F1.opExtrude","CAP_FACE",FACE,{"disambiguationData":[OSD([subQ5,subQ7,subQ8,subQ9,subQ4,subQ3,subQ2,subQ1,subQ6,subQ0,subQ10,subQ11])],"isStart":true})});}
            var sketch = newSketch(context, id + "F16", { "sketchPlane" : qUnion([Q0])});
            skArc(sketch, "E79.0", {"start": v(56.15, 48.18) * mm, "mid": v(0, 67.5) * mm, "end": v(-56.15, 48.18) * mm});
            skArc(sketch, "E79.1", {"start": v(-56.15, 48.18) * mm, "mid": v(-58.99, 44.68) * mm, "end": v(-60, 40.3) * mm});
            skLineSegment(sketch, "E79.2", {"start": v(-60, 40.3) * mm, "end": v(-60, -40.3) * mm});
            skArc(sketch, "E79.3", {"start": v(-60, -40.3) * mm, "mid": v(-58.99, -44.68) * mm, "end": v(-56.15, -48.18) * mm});
            skArc(sketch, "E79.4", {"start": v(-56.15, -48.18) * mm, "mid": v(0, -67.5) * mm, "end": v(56.15, -48.18) * mm});
            skArc(sketch, "E79.5", {"start": v(56.15, -48.18) * mm, "mid": v(58.99, -44.68) * mm, "end": v(60, -40.3) * mm});
            skLineSegment(sketch, "E79.6", {"start": v(60, 40.3) * mm, "end": v(60, -40.3) * mm});
            skArc(sketch, "E79.7", {"start": v(60, 40.3) * mm, "mid": v(58.99, 44.68) * mm, "end": v(56.15, 48.18) * mm});
            skCircle(sketch, "E79.8", {"center": v(60, 67.5) * mm, "radius": 4 * mm});
            skCircle(sketch, "E79.9", {"center": v(-60, 67.5) * mm, "radius": 4 * mm});
            skCircle(sketch, "E79.10", {"center": v(-60, -67.5) * mm, "radius": 4 * mm});
            skCircle(sketch, "E79.11", {"center": v(60, -67.5) * mm, "radius": 4 * mm});
            skLineSegment(sketch, "E79.12", {"start": v(-80, -80) * mm, "end": v(-80, 80) * mm});
            skArc(sketch, "E79.13", {"start": v(-70, 90) * mm, "mid": v(-77.07, 87.07) * mm, "end": v(-80, 80) * mm});
            skLineSegment(sketch, "E79.14", {"start": v(-70, 90) * mm, "end": v(70, 90) * mm});
            skArc(sketch, "E79.15", {"start": v(80, 80) * mm, "mid": v(77.07, 87.07) * mm, "end": v(70, 90) * mm});
            skLineSegment(sketch, "E79.16", {"start": v(80, -80) * mm, "end": v(80, 80) * mm});
            skArc(sketch, "E79.17", {"start": v(70, -90) * mm, "mid": v(77.07, -87.07) * mm, "end": v(80, -80) * mm});
            skLineSegment(sketch, "E79.18", {"start": v(-70, -90) * mm, "end": v(70, -90) * mm});
            skArc(sketch, "E79.19", {"start": v(-80, -80) * mm, "mid": v(-77.07, -87.07) * mm, "end": v(-70, -90) * mm});
            skLineSegment(sketch, "E80", {"start": v(0, 120) * mm, "end": v(0, 90) * mm});
            skPoint(sketch, "E80.startSnap0", {"position": v(0, 90) * mm});
            skLineSegment(sketch, "E81", {"start": v(0, 90) * mm, "end": v(0, 120) * mm});
            skCircle(sketch, "E82", {"center": v(0, 120) * mm, "radius": 6 * mm});
            skArc(sketch, "E83", {"start": v(15, 120) * mm, "mid": v(0, 135) * mm, "end": v(-15, 120) * mm});
            skLineSegment(sketch, "E84", {"start": v(15, 120) * mm, "end": v(15, 108) * mm});
            skLineSegment(sketch, "E85", {"start": v(37.02, 90) * mm, "end": v(15, 108) * mm});
            skLineSegment(sketch, "E86", {"start": v(-15, 120) * mm, "end": v(-15, 108) * mm});
            skLineSegment(sketch, "E87", {"start": v(-15, 108) * mm, "end": v(-37.55, 90) * mm});
            skPoint(sketch, "E88.MirrorP", {"position": v(0, -74.25) * mm});
            skPoint(sketch, "E89.MirrorP", {"position": v(0, -90) * mm});
            skLineSegment(sketch, "E90.MirrorCS", {"start": v(15, -120) * mm, "end": v(15, -108) * mm});
            skLineSegment(sketch, "E91.MirrorCS", {"start": v(-15, -120) * mm, "end": v(-15, -108) * mm});
            skArc(sketch, "E92.MirrorCS", {"start": v(15, -120) * mm, "mid": v(0, -135) * mm, "end": v(-15, -120) * mm});
            skCircle(sketch, "E93.MirrorC", {"center": v(0, -120) * mm, "radius": 6 * mm});
            skLineSegment(sketch, "E94.MirrorCS", {"start": v(-15, -108) * mm, "end": v(-37.55, -90) * mm});
            skLineSegment(sketch, "E95.MirrorCS", {"start": v(37.02, -90) * mm, "end": v(15, -108) * mm});
            skLineSegment(sketch, "E96.MirrorCS", {"start": v(0, -90) * mm, "end": v(0, -120) * mm});
            skSolve(sketch);
        }
        {
            var Q0;
            Q0=makeQuery(id+"F16.imprint","IMPRINT",FACE,{"disambiguationData":[TD([[makeQuery(id+"F16.imprint","IMPRINT",EDGE,{"derivedFrom":sQuery(id+"F16.wireOp",EDGE,"E79.0")}),-1.0]])]});
            var Q1;
            {var subQ13=sQuery(id+"F16.wireOp",EDGE,"E79.3");Q1=makeQuery(id+"F16.imprint","IMPRINT",FACE,{"disambiguationData":[TD([[makeQuery(id+"F16.imprint","IMPRINT",EDGE,{"derivedFrom":subQ13}),-1.0]])]});}
            var Q2;
            Q2=makeQuery(id+"F16.imprint","IMPRINT",FACE,{"disambiguationData":[TD([[makeQuery(id+"F16.imprint","IMPRINT",EDGE,{"derivedFrom":sQuery(id+"F16.wireOp",EDGE,"E82")}),-1.0]])]});
            var Q3;
            Q3=makeQuery(id+"F16.imprint","IMPRINT",FACE,{"disambiguationData":[TD([[makeQuery(id+"F16.imprint","IMPRINT",EDGE,{"derivedFrom":sQuery(id+"F16.wireOp",EDGE,"478d619f-8ca0-4a5e-bb88-79d9751e5b221.MirrorCS")}),-1.0]])]});
            var Q4;
            Q4=makeQuery(id+"F2.opExtrude","CAP_FACE",FACE,{"disambiguationData":[OSD([sQuery(id+"F0.wireOp",EDGE,"E12"),sQuery(id+"F0.wireOp",EDGE,"E13"),sQuery(id+"F0.wireOp",EDGE,"E14"),sQuery(id+"F0.wireOp",EDGE,"E15"),sQuery(id+"F0.wireOp",EDGE,"E17.filletArc"),sQuery(id+"F0.wireOp",EDGE,"E18.filletArc"),sQuery(id+"F0.wireOp",EDGE,"E19.filletArc"),sQuery(id+"F0.wireOp",EDGE,"E20.filletArc"),sQuery(id+"F0.wireOp",EDGE,"E25.0"),sQuery(id+"F0.wireOp",EDGE,"E25.1"),sQuery(id+"F0.wireOp",EDGE,"E25.2"),sQuery(id+"F0.wireOp",EDGE,"E25.3"),sQuery(id+"F0.wireOp",EDGE,"E25.4"),sQuery(id+"F0.wireOp",EDGE,"E25.5"),sQuery(id+"F0.wireOp",EDGE,"E25.6"),sQuery(id+"F0.wireOp",EDGE,"E25.7")])],"isStart":false});
            extrude(context, id + "F17", {"entities" : qUnion([Q0, Q1, Q2, Q3]), "endBound" : BoundingType.UP_TO_SURFACE, "endBoundEntityFace" : qUnion([Q4]), "depth" : 25 * mm});
        }
        {
            var Q0;
            Q0 = qSketchRegion(id + "F16", true);
            var Q1;
            Q1=makeQuery(id+"F2.opExtrude","CAP_FACE",FACE,{"disambiguationData":[OSD([sQuery(id+"F0.wireOp",EDGE,"E12"),sQuery(id+"F0.wireOp",EDGE,"E13"),sQuery(id+"F0.wireOp",EDGE,"E14"),sQuery(id+"F0.wireOp",EDGE,"E15"),sQuery(id+"F0.wireOp",EDGE,"E17.filletArc"),sQuery(id+"F0.wireOp",EDGE,"E18.filletArc"),sQuery(id+"F0.wireOp",EDGE,"E19.filletArc"),sQuery(id+"F0.wireOp",EDGE,"E20.filletArc"),sQuery(id+"F0.wireOp",EDGE,"E25.0"),sQuery(id+"F0.wireOp",EDGE,"E25.1"),sQuery(id+"F0.wireOp",EDGE,"E25.2"),sQuery(id+"F0.wireOp",EDGE,"E25.3"),sQuery(id+"F0.wireOp",EDGE,"E25.4"),sQuery(id+"F0.wireOp",EDGE,"E25.5"),sQuery(id+"F0.wireOp",EDGE,"E25.6"),sQuery(id+"F0.wireOp",EDGE,"E25.7")])],"isStart":false});
            extrude(context, id + "F18", {"entities" : qUnion([Q0]), "endBound" : BoundingType.UP_TO_SURFACE, "endBoundEntityFace" : qUnion([Q1]), "depth" : 25 * mm});
        }
        {
            var Q0;
            Q0=makeQuery(id+"F16.imprint","IMPRINT",FACE,{"disambiguationData":[TD([[makeQuery(id+"F16.imprint","IMPRINT",EDGE,{"derivedFrom":sQuery(id+"F16.wireOp",EDGE,"E82")}),-1.0]])]});
            var Q1;
            Q1=makeQuery(id+"F16.imprint","IMPRINT",FACE,{"disambiguationData":[TD([[makeQuery(id+"F16.imprint","IMPRINT",EDGE,{"derivedFrom":sQuery(id+"F16.wireOp",EDGE,"E79.0")}),-1.0]])]});
            var Q2;
            Q2=makeQuery(id+"F16.imprint","IMPRINT",FACE,{"disambiguationData":[TD([[makeQuery(id+"F16.imprint","IMPRINT",EDGE,{"derivedFrom":sQuery(id+"F16.wireOp",EDGE,"E90.MirrorCS")}),1.0]])]});
            var Q3;
            Q3=makeQuery(id+"F2.opExtrude","CAP_FACE",FACE,{"disambiguationData":[OSD([sQuery(id+"F0.wireOp",EDGE,"E12"),sQuery(id+"F0.wireOp",EDGE,"E13"),sQuery(id+"F0.wireOp",EDGE,"E14"),sQuery(id+"F0.wireOp",EDGE,"E15"),sQuery(id+"F0.wireOp",EDGE,"E17.filletArc"),sQuery(id+"F0.wireOp",EDGE,"E18.filletArc"),sQuery(id+"F0.wireOp",EDGE,"E19.filletArc"),sQuery(id+"F0.wireOp",EDGE,"E20.filletArc"),sQuery(id+"F0.wireOp",EDGE,"E25.0"),sQuery(id+"F0.wireOp",EDGE,"E25.1"),sQuery(id+"F0.wireOp",EDGE,"E25.2"),sQuery(id+"F0.wireOp",EDGE,"E25.3"),sQuery(id+"F0.wireOp",EDGE,"E25.4"),sQuery(id+"F0.wireOp",EDGE,"E25.5"),sQuery(id+"F0.wireOp",EDGE,"E25.6"),sQuery(id+"F0.wireOp",EDGE,"E25.7")])],"isStart":false});
            extrude(context, id + "F19", {"entities" : qUnion([Q0, Q1, Q2]), "endBound" : BoundingType.UP_TO_SURFACE, "endBoundEntityFace" : qUnion([Q3]), "depth" : 25 * mm});
        }
        {
            var Q0;
            Q0=makeQuery(id+"F17.opExtrude","SWEPT_BODY",BODY,{"disambiguationData":[OSD([sQuery(id+"F16.wireOp",EDGE,"E79.0"),sQuery(id+"F16.wireOp",EDGE,"E79.1"),sQuery(id+"F16.wireOp",EDGE,"E79.2"),sQuery(id+"F16.wireOp",EDGE,"E79.3"),sQuery(id+"F16.wireOp",EDGE,"E79.4"),sQuery(id+"F16.wireOp",EDGE,"E79.5"),sQuery(id+"F16.wireOp",EDGE,"E79.6"),sQuery(id+"F16.wireOp",EDGE,"E79.7"),sQuery(id+"F16.wireOp",EDGE,"E79.8"),sQuery(id+"F16.wireOp",EDGE,"E79.9"),sQuery(id+"F16.wireOp",EDGE,"E79.10"),sQuery(id+"F16.wireOp",EDGE,"E79.11"),sQuery(id+"F16.wireOp",EDGE,"E79.12"),sQuery(id+"F16.wireOp",EDGE,"E79.13"),sQuery(id+"F16.wireOp",EDGE,"E79.14"),sQuery(id+"F16.wireOp",EDGE,"E79.15"),sQuery(id+"F16.wireOp",EDGE,"E79.16"),sQuery(id+"F16.wireOp",EDGE,"E79.17"),sQuery(id+"F16.wireOp",EDGE,"E79.18"),sQuery(id+"F16.wireOp",EDGE,"E79.19"),sQuery(id+"F16.wireOp",EDGE,"E82"),sQuery(id+"F16.wireOp",EDGE,"E83"),sQuery(id+"F16.wireOp",EDGE,"E84"),sQuery(id+"F16.wireOp",EDGE,"E85"),sQuery(id+"F16.wireOp",EDGE,"E86"),sQuery(id+"F16.wireOp",EDGE,"E87")])]});
            deleteBodies(context, id + "F20", {"entities" : qUnion([Q0])});
        }
    });
